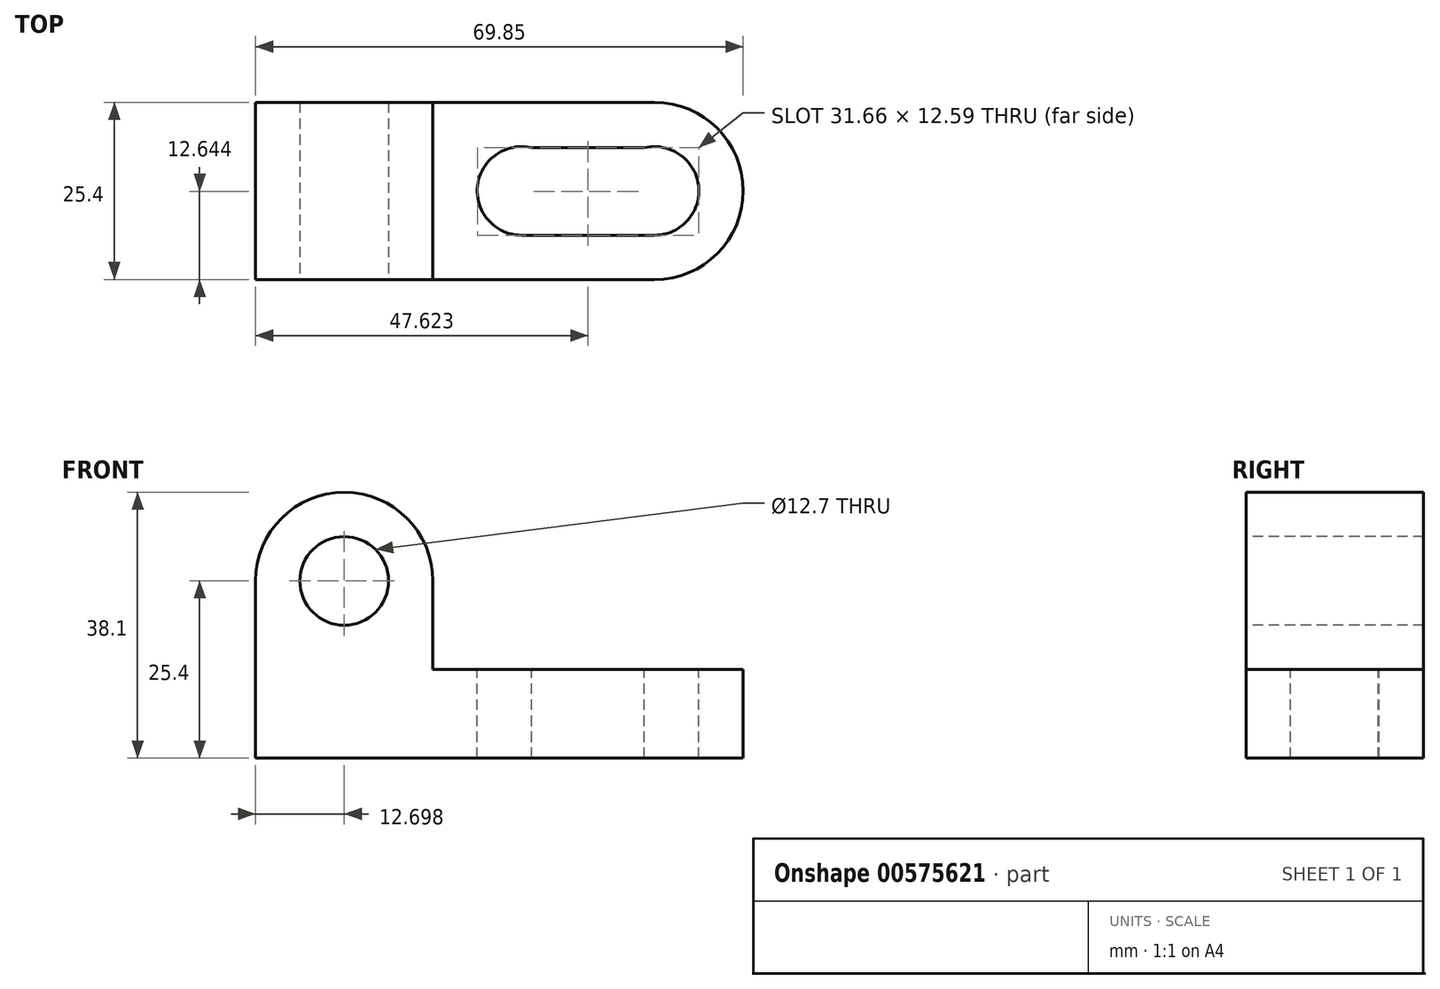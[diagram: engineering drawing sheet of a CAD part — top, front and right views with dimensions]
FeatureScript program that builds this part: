
annotation { "Feature Type Name" : "Feature", "Feature Type Description" : "" }
export const myFeature = defineFeature(function(context is Context, id is Id, definition is map)
    precondition{}
    {
        {
            var Q0;
            Q0=qCreatedBy(makeId("Front.planeOp"),FACE);
            var sketch = newSketch(context, id + "F0", { "sketchPlane" : qUnion([Q0])});
            skLineSegment(sketch, "E0", {"start": v(-76.71, 54.3) * mm, "end": v(-76.71, 16.2) * mm});
            skLineSegment(sketch, "E1", {"start": v(-76.71, 16.2) * mm, "end": v(-6.86, 16.2) * mm});
            skLineSegment(sketch, "E2", {"start": v(-6.86, 16.2) * mm, "end": v(-6.86, 28.9) * mm});
            skLineSegment(sketch, "E3", {"start": v(-6.86, 28.9) * mm, "end": v(-51.31, 28.9) * mm});
            skLineSegment(sketch, "E4", {"start": v(-51.31, 28.9) * mm, "end": v(-51.31, 54.3) * mm});
            skLineSegment(sketch, "E5", {"start": v(-51.31, 54.3) * mm, "end": v(-76.71, 54.3) * mm});
            skSolve(sketch);
        }
        {
            var Q0;
            Q0=makeQuery(id+"F0.imprint","IMPRINT",FACE,{"disambiguationData":[TD([[makeQuery(id+"F0.imprint","IMPRINT",EDGE,{"derivedFrom":sQuery(id+"F0.wireOp",EDGE,"E0")}),1.0]])]});
            extrude(context, id + "F1", {"entities" : qUnion([Q0]), "depth" : 25.4 * mm, "offsetDistance" : 25.4 * mm});
        }
        {
            var Q0;
            Q0=makeQuery(id+"F1.opExtrude","CAP_FACE",FACE,{"disambiguationData":[OSD([sQuery(id+"F0.wireOp",EDGE,"E0"),sQuery(id+"F0.wireOp",EDGE,"E1"),sQuery(id+"F0.wireOp",EDGE,"E2"),sQuery(id+"F0.wireOp",EDGE,"E3"),sQuery(id+"F0.wireOp",EDGE,"E4"),sQuery(id+"F0.wireOp",EDGE,"E5")])],"isStart":false});
            var sketch = newSketch(context, id + "F2", { "sketchPlane" : qUnion([Q0])});
            skCircle(sketch, "E6", {"center": v(-64.01, 41.6) * mm, "radius": 12.7 * mm});
            skSolve(sketch);
        }
        {
            var Q0;
            {var subQ0=sQuery(id+"F2.wireOp",EDGE,"E6");var subQ1=makeQuery(id+"F2.imprint","INTERSECT",VERTEX,{"derivedFrom":[makeQuery(id+"F1.opExtrude","CAP_EDGE",EDGE,{"disambiguationData":[OSD([sQuery(id+"F0.wireOp",EDGE,"E5")])],"isStart":false}),subQ0]});Q0=makeQuery(id+"F2.imprint","IMPRINT",FACE,{"disambiguationData":[TD([[makeQuery(id+"F2.imprint","IMPRINT",EDGE,{"disambiguationData":[TD([[subQ1,1.0]])],"derivedFrom":subQ0}),1.0]])]});}
            var sketch = newSketch(context, id + "F3", { "sketchPlane" : qUnion([Q0])});
            skCircle(sketch, "E7", {"center": v(-64.01, 41.6) * mm, "radius": 6.35 * mm});
            skSolve(sketch);
        }
        {
            var Q0;
            {var subQ0=sQuery(id+"F2.wireOp",EDGE,"E6");var subQ1=makeQuery(id+"F1.opExtrude","CAP_EDGE",EDGE,{"disambiguationData":[OSD([sQuery(id+"F0.wireOp",EDGE,"E5")])],"isStart":false});var subQ2=makeQuery(id+"F2.imprint","INTERSECT",VERTEX,{"derivedFrom":[subQ1,subQ0]});Q0=makeQuery(id+"F2.imprint","IMPRINT",FACE,{"disambiguationData":[TD([[makeQuery(id+"F2.imprint","IMPRINT",EDGE,{"disambiguationData":[TD([[subQ2,-1.0]])],"derivedFrom":subQ0}),-1.0]])]});}
            var Q1;
            {var subQ0=sQuery(id+"F2.wireOp",EDGE,"E6");var subQ1=makeQuery(id+"F1.opExtrude","CAP_EDGE",EDGE,{"disambiguationData":[OSD([sQuery(id+"F0.wireOp",EDGE,"E5")])],"isStart":false});var subQ2=makeQuery(id+"F2.imprint","INTERSECT",VERTEX,{"derivedFrom":[subQ1,subQ0]});Q1=makeQuery(id+"F2.imprint","IMPRINT",FACE,{"disambiguationData":[TD([[makeQuery(id+"F2.imprint","IMPRINT",EDGE,{"disambiguationData":[TD([[subQ2,1.0]])],"derivedFrom":subQ0}),-1.0]])]});}
            extrude(context, id + "F4", {"entities" : qUnion([Q0, Q1]), "operationType" : NewBodyOperationType.REMOVE, "endBound" : BoundingType.THROUGH_ALL, "oppositeDirection" : true, "depth" : 25.4 * mm, "offsetDistance" : 25.4 * mm});
        }
        {
            var Q0;
            Q0=makeQuery(id+"F3.imprint","IMPRINT",FACE,{"disambiguationData":[TD([[makeQuery(id+"F3.imprint","IMPRINT",EDGE,{"derivedFrom":sQuery(id+"F3.wireOp",EDGE,"E7")}),1.0]])]});
            extrude(context, id + "F5", {"entities" : qUnion([Q0]), "operationType" : NewBodyOperationType.REMOVE, "endBound" : BoundingType.THROUGH_ALL, "oppositeDirection" : true, "depth" : 25.4 * mm, "offsetDistance" : 25.4 * mm});
        }
        {
            var Q0;
            Q0=makeQuery(id+"F1.opExtrude","SWEPT_FACE",FACE,{"disambiguationData":[OSD([sQuery(id+"F0.wireOp",EDGE,"E3")])]});
            var sketch = newSketch(context, id + "F6", { "sketchPlane" : qUnion([Q0])});
            skCircle(sketch, "E8", {"center": v(-38.61, -12.7) * mm, "radius": 6.35 * mm});
            skCircle(sketch, "E9", {"center": v(-19.56, -12.7) * mm, "radius": 6.35 * mm});
            skLineSegment(sketch, "E10", {"start": v(-38.61, -6.35) * mm, "end": v(-19.56, -6.35) * mm});
            skLineSegment(sketch, "E11", {"start": v(-38.61, -19.05) * mm, "end": v(-19.56, -19.05) * mm});
            skSolve(sketch);
        }
        {
            var Q0;
            Q0=makeQuery(id+"F6.imprint","IMPRINT",FACE,{"disambiguationData":[TD([[makeQuery(id+"F6.imprint","IMPRINT",EDGE,{"derivedFrom":sQuery(id+"F6.wireOp",EDGE,"E8")}),-1.0]])]});
            var sketch = newSketch(context, id + "F7", { "sketchPlane" : qUnion([Q0])});
            skLineSegment(sketch, "E12", {"start": v(-19.56, -19.22) * mm, "end": v(-38.61, -19.22) * mm});
            skLineSegment(sketch, "E13", {"start": v(-38.61, -6.52) * mm, "end": v(-19.56, -6.52) * mm});
            skSolve(sketch);
        }
        {
            var Q0;
            Q0=makeQuery(id+"F6.imprint","IMPRINT",FACE,{"disambiguationData":[TD([[makeQuery(id+"F6.imprint","IMPRINT",EDGE,{"derivedFrom":sQuery(id+"F6.wireOp",EDGE,"E8")}),1.0]])]});
            var Q1;
            Q1=makeQuery(id+"F6.imprint","IMPRINT",FACE,{"disambiguationData":[TD([[makeQuery(id+"F6.imprint","IMPRINT",EDGE,{"derivedFrom":sQuery(id+"F6.wireOp",EDGE,"E9")}),1.0]])]});
            extrude(context, id + "F8", {"entities" : qUnion([Q0, Q1]), "operationType" : NewBodyOperationType.REMOVE, "endBound" : BoundingType.THROUGH_ALL, "oppositeDirection" : true, "depth" : 25.4 * mm, "offsetDistance" : 25.4 * mm});
        }
        {
            var Q0;
            {var subQ3=sQuery(id+"F6.wireOp",EDGE,"E11");var subQ9=makeQuery(id+"F6.imprint","IMPRINT",EDGE,{"derivedFrom":subQ3});Q0=makeQuery(id+"F7.imprint","IMPRINT",FACE,{"disambiguationData":[TD([[makeQuery(id+"F7.imprint","IMPRINT",EDGE,{"derivedFrom":subQ9}),1.0]])]});}
            extrude(context, id + "F9", {"entities" : qUnion([Q0]), "operationType" : NewBodyOperationType.REMOVE, "endBound" : BoundingType.THROUGH_ALL, "oppositeDirection" : true, "depth" : 25.4 * mm, "offsetDistance" : 25.4 * mm});
        }
        {
            var Q0;
            Q0=makeQuery(id+"F1.opExtrude","SWEPT_FACE",FACE,{"disambiguationData":[OSD([sQuery(id+"F0.wireOp",EDGE,"E3")])]});
            var sketch = newSketch(context, id + "F10", { "sketchPlane" : qUnion([Q0])});
            skCircle(sketch, "E14", {"center": v(-19.56, -12.7) * mm, "radius": 12.7 * mm});
            skSolve(sketch);
        }
        {
            var Q0;
            {var subQ0=sQuery(id+"F10.wireOp",EDGE,"E14");var subQ1=sQuery(id+"F0.wireOp",EDGE,"E3");var subQ2=makeQuery(id+"F1.opExtrude","CAP_EDGE",EDGE,{"disambiguationData":[OSD([subQ1])],"isStart":true});var subQ3=makeQuery(id+"F10.imprint","INTERSECT",VERTEX,{"derivedFrom":[subQ2,subQ0]});Q0=makeQuery(id+"F10.imprint","IMPRINT",FACE,{"disambiguationData":[TD([[makeQuery(id+"F10.imprint","IMPRINT",EDGE,{"disambiguationData":[TD([[subQ3,1.0]])],"derivedFrom":subQ0}),-1.0]])]});}
            var Q1;
            {var subQ0=sQuery(id+"F10.wireOp",EDGE,"E14");var subQ1=sQuery(id+"F0.wireOp",EDGE,"E3");var subQ4=makeQuery(id+"F1.opExtrude","CAP_EDGE",EDGE,{"disambiguationData":[OSD([subQ1])],"isStart":false});var subQ5=makeQuery(id+"F10.imprint","INTERSECT",VERTEX,{"derivedFrom":[subQ4,subQ0]});Q1=makeQuery(id+"F10.imprint","IMPRINT",FACE,{"disambiguationData":[TD([[makeQuery(id+"F10.imprint","IMPRINT",EDGE,{"disambiguationData":[TD([[subQ5,-1.0]])],"derivedFrom":subQ0}),-1.0]])]});}
            extrude(context, id + "F11", {"entities" : qUnion([Q0, Q1]), "operationType" : NewBodyOperationType.REMOVE, "endBound" : BoundingType.THROUGH_ALL, "oppositeDirection" : true, "depth" : 25.4 * mm, "offsetDistance" : 25.4 * mm});
        }
    });
